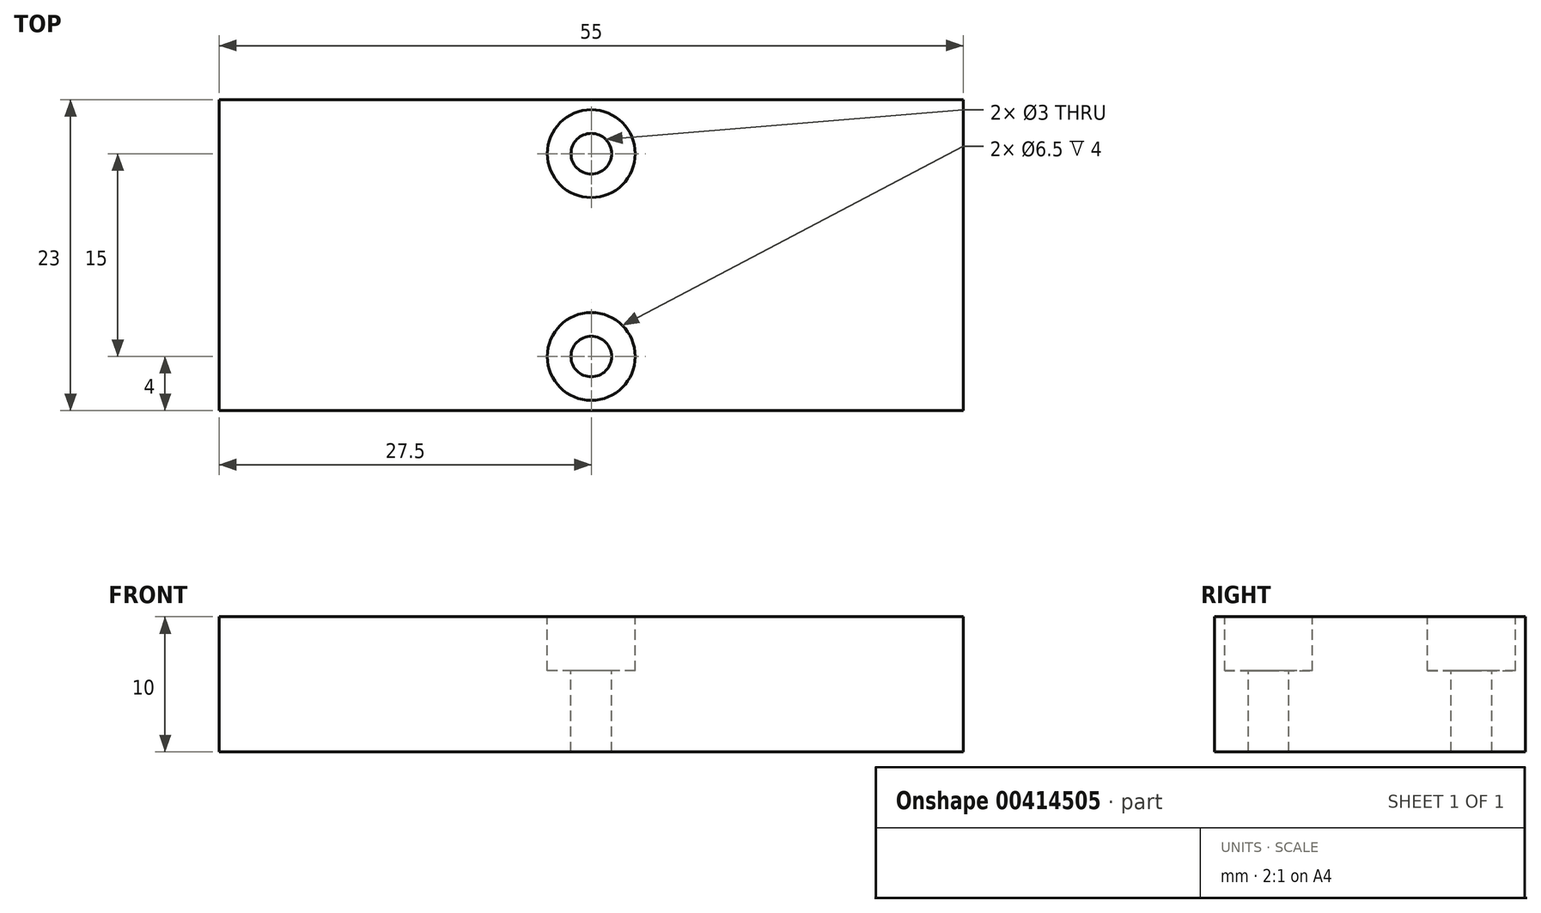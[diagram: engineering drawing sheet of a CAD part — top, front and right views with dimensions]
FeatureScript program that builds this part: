
annotation { "Feature Type Name" : "Feature", "Feature Type Description" : "" }
export const myFeature = defineFeature(function(context is Context, id is Id, definition is map)
    precondition{}
    {
        {
            var Q0;
            Q0=qCreatedBy(makeId("Top.planeOp"),FACE);
            var sketch = newSketch(context, id + "F0", { "sketchPlane" : qUnion([Q0])});
            skLineSegment(sketch, "E0.bottom", {"start": v(-27.5, 11.5) * mm, "end": v(27.5, 11.5) * mm});
            skLineSegment(sketch, "E0.top", {"start": v(-27.5, -11.5) * mm, "end": v(27.5, -11.5) * mm});
            skLineSegment(sketch, "E0.left", {"start": v(-27.5, 11.5) * mm, "end": v(-27.5, -11.5) * mm});
            skLineSegment(sketch, "E0.right", {"start": v(27.5, 11.5) * mm, "end": v(27.5, -11.5) * mm});
            skPoint(sketch, "E0.middle", {"position": v(0, 0) * mm});
            skSolve(sketch);
        }
        {
            var Q0;
            Q0=makeQuery(id+"F0.imprint","IMPRINT",FACE,{"disambiguationData":[TD([[makeQuery(id+"F0.imprint","IMPRINT",EDGE,{"derivedFrom":sQuery(id+"F0.wireOp",EDGE,"E0.bottom")}),-1.0]])]});
            extrude(context, id + "F1", {"entities" : qUnion([Q0]), "depth" : 10 * mm});
        }
        {
            var Q0;
            Q0=makeQuery(id+"F1.opExtrude","CAP_FACE",FACE,{"disambiguationData":[OSD([sQuery(id+"F0.wireOp",EDGE,"E0.bottom"),sQuery(id+"F0.wireOp",EDGE,"E0.top"),sQuery(id+"F0.wireOp",EDGE,"E0.left"),sQuery(id+"F0.wireOp",EDGE,"E0.right")])],"isStart":false});
            var sketch = newSketch(context, id + "F2", { "sketchPlane" : qUnion([Q0])});
            skLineSegment(sketch, "E1", {"start": v(0, 7.5) * mm, "end": v(0, -7.5) * mm, "construction": true});
            skPoint(sketch, "E2", {"position": v(0, 7.5) * mm});
            skPoint(sketch, "E3", {"position": v(0, -7.5) * mm});
            skSolve(sketch);
        }
        {
            var Q0;
            Q0=sQuery(id+"F2.wireOp",VERTEX,"E2");
            var Q1;
            Q1=sQuery(id+"F2.wireOp",VERTEX,"E3");
            var Q2;
            Q2=makeQuery(id+"F1.opExtrude","SWEPT_BODY",BODY,{"disambiguationData":[OSD([sQuery(id+"F0.wireOp",EDGE,"E0.bottom"),sQuery(id+"F0.wireOp",EDGE,"E0.top"),sQuery(id+"F0.wireOp",EDGE,"E0.left"),sQuery(id+"F0.wireOp",EDGE,"E0.right")])]});
            hole(context, id + "F3", {"style" : HoleStyle.C_BORE, "endStyle" : HoleEndStyle.THROUGH, "standardTappedOrClearance" : lookupTablePath({ "standard" : "ISO", "size" : "3", "type" : "Drilled" }), "standardBlindInLast" : lookupTablePath({ "standard" : "ISO", "size" : "3", "type" : "Drilled" }), "holeDiameter" : 3 * mm, "cBoreDiameter" : 6.5 * mm, "cBoreDepth" : 4 * mm, "tappedDepth" : 4 * mm, "tapClearance" : 2, "startFromSketch" : true, "locations" : qUnion([Q0, Q1]), "scope" : qUnion([Q2])});
        }
    });
